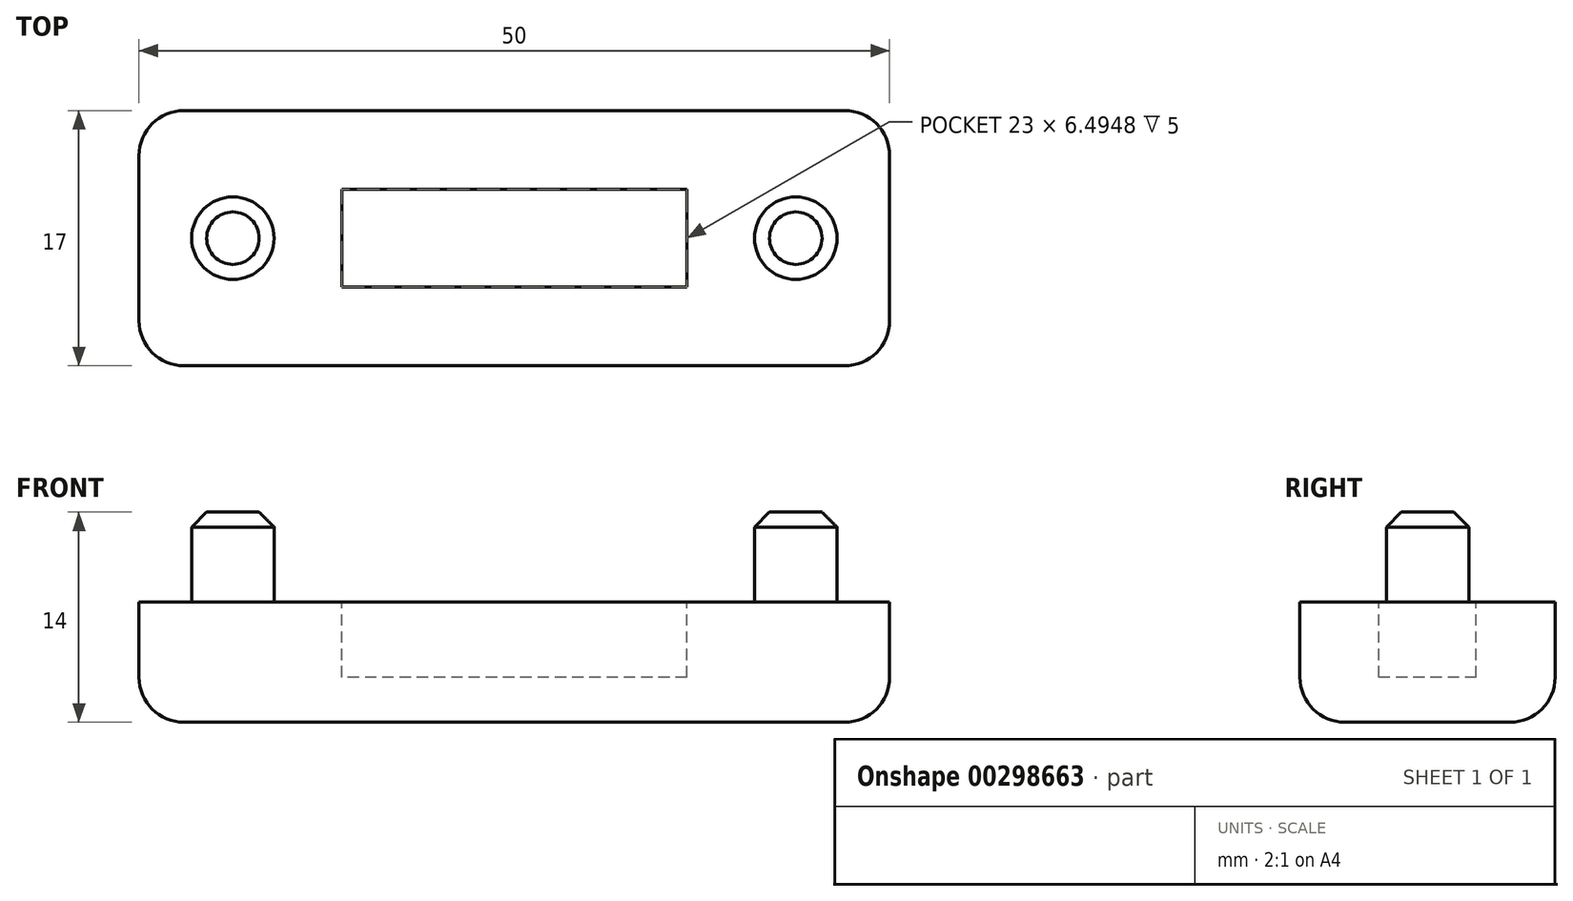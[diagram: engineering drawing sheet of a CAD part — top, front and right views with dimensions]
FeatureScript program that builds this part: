
annotation { "Feature Type Name" : "Feature", "Feature Type Description" : "" }
export const myFeature = defineFeature(function(context is Context, id is Id, definition is map)
    precondition{}
    {
        {
            var Q0;
            Q0=qCreatedBy(makeId("Top.planeOp"),FACE);
            var sketch = newSketch(context, id + "F0", { "sketchPlane" : qUnion([Q0])});
            skLineSegment(sketch, "E0.bottom", {"start": v(25, -8.5) * mm, "end": v(-25, -8.5) * mm});
            skLineSegment(sketch, "E0.top", {"start": v(25, 8.5) * mm, "end": v(-25, 8.5) * mm});
            skLineSegment(sketch, "E0.left", {"start": v(25, -8.5) * mm, "end": v(25, 8.5) * mm});
            skLineSegment(sketch, "E0.right", {"start": v(-25, -8.5) * mm, "end": v(-25, 8.5) * mm});
            skPoint(sketch, "E0.middle", {"position": v(0, 0) * mm});
            skSolve(sketch);
        }
        {
            var Q0;
            Q0=makeQuery(id+"F0.imprint","IMPRINT",FACE,{"disambiguationData":[TD([[makeQuery(id+"F0.imprint","IMPRINT",EDGE,{"derivedFrom":sQuery(id+"F0.wireOp",EDGE,"E0.bottom")}),-1.0]])]});
            extrude(context, id + "F1", {"entities" : qUnion([Q0]), "depth" : 8 * mm});
        }
        {
            var Q0;
            Q0=makeQuery(id+"F1.opExtrude","CAP_FACE",FACE,{"disambiguationData":[OSD([sQuery(id+"F0.wireOp",EDGE,"E0.bottom"),sQuery(id+"F0.wireOp",EDGE,"E0.top"),sQuery(id+"F0.wireOp",EDGE,"E0.left"),sQuery(id+"F0.wireOp",EDGE,"E0.right")])],"isStart":false});
            var sketch = newSketch(context, id + "F2", { "sketchPlane" : qUnion([Q0])});
            skLineSegment(sketch, "E1.bottom", {"start": v(25, -8.5) * mm, "end": v(-25, -8.5) * mm});
            skLineSegment(sketch, "E1.top", {"start": v(25, 8.5) * mm, "end": v(-25, 8.5) * mm});
            skLineSegment(sketch, "E1.left", {"start": v(25, -8.5) * mm, "end": v(25, 8.5) * mm});
            skLineSegment(sketch, "E1.right", {"start": v(-25, -8.5) * mm, "end": v(-25, 8.5) * mm});
            skPoint(sketch, "E1.middle", {"position": v(0, 0) * mm});
            skCircle(sketch, "E2", {"center": v(-18.75, 0) * mm, "radius": 2.75 * mm});
            skCircle(sketch, "E3", {"center": v(18.75, 0) * mm, "radius": 2.75 * mm});
            skLineSegment(sketch, "E4.bottom", {"start": v(11.5, 3.25) * mm, "end": v(-11.5, 3.25) * mm});
            skLineSegment(sketch, "E4.top", {"start": v(11.5, -3.25) * mm, "end": v(-11.5, -3.25) * mm});
            skLineSegment(sketch, "E4.left", {"start": v(11.5, 3.25) * mm, "end": v(11.5, -3.25) * mm});
            skLineSegment(sketch, "E4.right", {"start": v(-11.5, 3.25) * mm, "end": v(-11.5, -3.25) * mm});
            skSolve(sketch);
        }
        {
            var Q0;
            Q0=makeQuery(id+"F2.imprint","IMPRINT",FACE,{"disambiguationData":[TD([[makeQuery(id+"F2.imprint","IMPRINT",EDGE,{"derivedFrom":sQuery(id+"F2.wireOp",EDGE,"E2")}),1.0]])]});
            var Q1;
            Q1=makeQuery(id+"F2.imprint","IMPRINT",FACE,{"disambiguationData":[TD([[makeQuery(id+"F2.imprint","IMPRINT",EDGE,{"derivedFrom":sQuery(id+"F2.wireOp",EDGE,"E3")}),1.0]])]});
            extrude(context, id + "F3", {"entities" : qUnion([Q0, Q1]), "operationType" : NewBodyOperationType.ADD, "depth" : 6 * mm});
        }
        {
            var Q0;
            Q0=makeQuery(id+"F2.imprint","IMPRINT",FACE,{"disambiguationData":[TD([[makeQuery(id+"F2.imprint","IMPRINT",EDGE,{"derivedFrom":sQuery(id+"F2.wireOp",EDGE,"E4.bottom")}),1.0]])]});
            extrude(context, id + "F4", {"entities" : qUnion([Q0]), "operationType" : NewBodyOperationType.REMOVE, "oppositeDirection" : true, "depth" : 5 * mm});
        }
        {
            var Q0;
            Q0=makeQuery(id+"F1.opExtrude","SWEPT_EDGE",EDGE,{"disambiguationData":[OSD([sQuery(id+"F0.wireOp",EDGE,"E0.bottom"),sQuery(id+"F0.wireOp",EDGE,"E0.right")])]});
            var Q1;
            Q1=makeQuery(id+"F1.opExtrude","SWEPT_EDGE",EDGE,{"disambiguationData":[OSD([sQuery(id+"F0.wireOp",EDGE,"E0.bottom"),sQuery(id+"F0.wireOp",EDGE,"E0.left")])]});
            var Q2;
            Q2=makeQuery(id+"F1.opExtrude","SWEPT_EDGE",EDGE,{"disambiguationData":[OSD([sQuery(id+"F0.wireOp",EDGE,"E0.top"),sQuery(id+"F0.wireOp",EDGE,"E0.right")])]});
            var Q3;
            Q3=makeQuery(id+"F1.opExtrude","SWEPT_EDGE",EDGE,{"disambiguationData":[OSD([sQuery(id+"F0.wireOp",EDGE,"E0.top"),sQuery(id+"F0.wireOp",EDGE,"E0.left")])]});
            var Q4;
            Q4=makeQuery(id+"F1.opExtrude","CAP_EDGE",EDGE,{"disambiguationData":[OSD([sQuery(id+"F0.wireOp",EDGE,"E0.top")])],"isStart":true});
            var Q5;
            Q5=makeQuery(id+"F1.opExtrude","CAP_EDGE",EDGE,{"disambiguationData":[OSD([sQuery(id+"F0.wireOp",EDGE,"E0.left")])],"isStart":true});
            var Q6;
            Q6=makeQuery(id+"F1.opExtrude","CAP_EDGE",EDGE,{"disambiguationData":[OSD([sQuery(id+"F0.wireOp",EDGE,"E0.bottom")])],"isStart":true});
            var Q7;
            Q7=makeQuery(id+"F1.opExtrude","CAP_EDGE",EDGE,{"disambiguationData":[OSD([sQuery(id+"F0.wireOp",EDGE,"E0.right")])],"isStart":true});
            fillet(context, id + "F5", {"entities" : qUnion([Q0, Q1, Q2, Q3, Q4, Q5, Q6, Q7]), "radius" : 3 * mm, "tangentPropagation" : true, "allowEdgeOverflow" : false});
        }
        {
            var Q0;
            Q0=makeQuery(id+"F3.opExtrude","CAP_EDGE",EDGE,{"disambiguationData":[OSD([sQuery(id+"F2.wireOp",EDGE,"E2")])],"isStart":false});
            var Q1;
            Q1=makeQuery(id+"F3.opExtrude","CAP_EDGE",EDGE,{"disambiguationData":[OSD([sQuery(id+"F2.wireOp",EDGE,"E3")])],"isStart":false});
            chamfer(context, id + "F6", {"entities" : qUnion([Q0, Q1]), "width" : 1 * mm, "tangentPropagation" : true});
        }
    });
